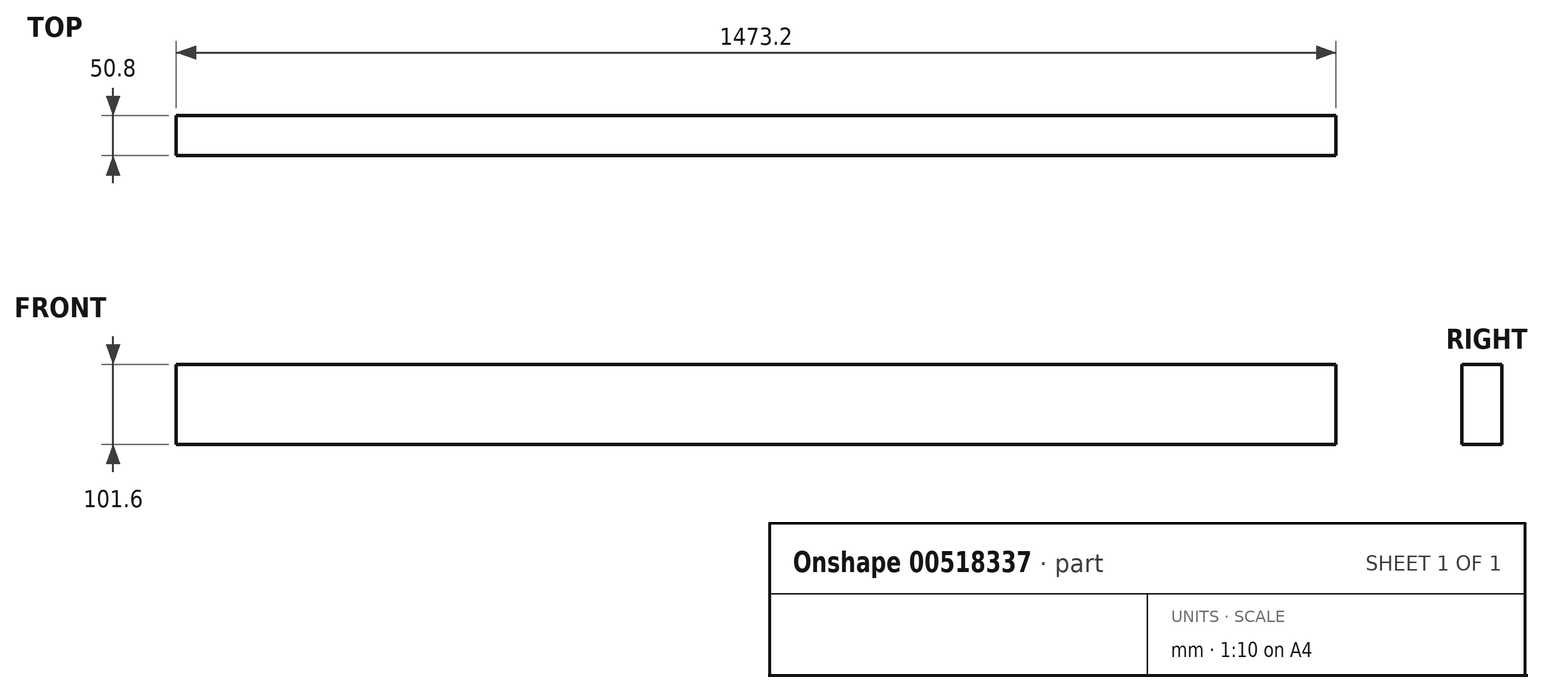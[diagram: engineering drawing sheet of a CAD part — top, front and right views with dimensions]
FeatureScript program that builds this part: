
annotation { "Feature Type Name" : "Feature", "Feature Type Description" : "" }
export const myFeature = defineFeature(function(context is Context, id is Id, definition is map)
    precondition{}
    {
        {
            var Q0;
            Q0=qCreatedBy(makeId("Top.planeOp"),FACE);
            var sketch = newSketch(context, id + "F0", { "sketchPlane" : qUnion([Q0])});
            skLineSegment(sketch, "E0.bottom", {"start": v(-736.6, 25.4) * mm, "end": v(736.6, 25.4) * mm});
            skLineSegment(sketch, "E0.top", {"start": v(-736.6, -25.4) * mm, "end": v(736.6, -25.4) * mm});
            skLineSegment(sketch, "E0.left", {"start": v(-736.6, 25.4) * mm, "end": v(-736.6, -25.4) * mm});
            skLineSegment(sketch, "E0.right", {"start": v(736.6, 25.4) * mm, "end": v(736.6, -25.4) * mm});
            skPoint(sketch, "E0.middle", {"position": v(0, 0) * mm});
            skSolve(sketch);
        }
        {
            var Q0;
            Q0=makeQuery(id+"F0.imprint","IMPRINT",FACE,{"disambiguationData":[TD([[makeQuery(id+"F0.imprint","IMPRINT",EDGE,{"derivedFrom":sQuery(id+"F0.wireOp",EDGE,"E0.bottom")}),-1.0]])]});
            extrude(context, id + "F1", {"entities" : qUnion([Q0]), "depth" : 101.6 * mm, "offsetDistance" : 25.4 * mm});
        }
    });
